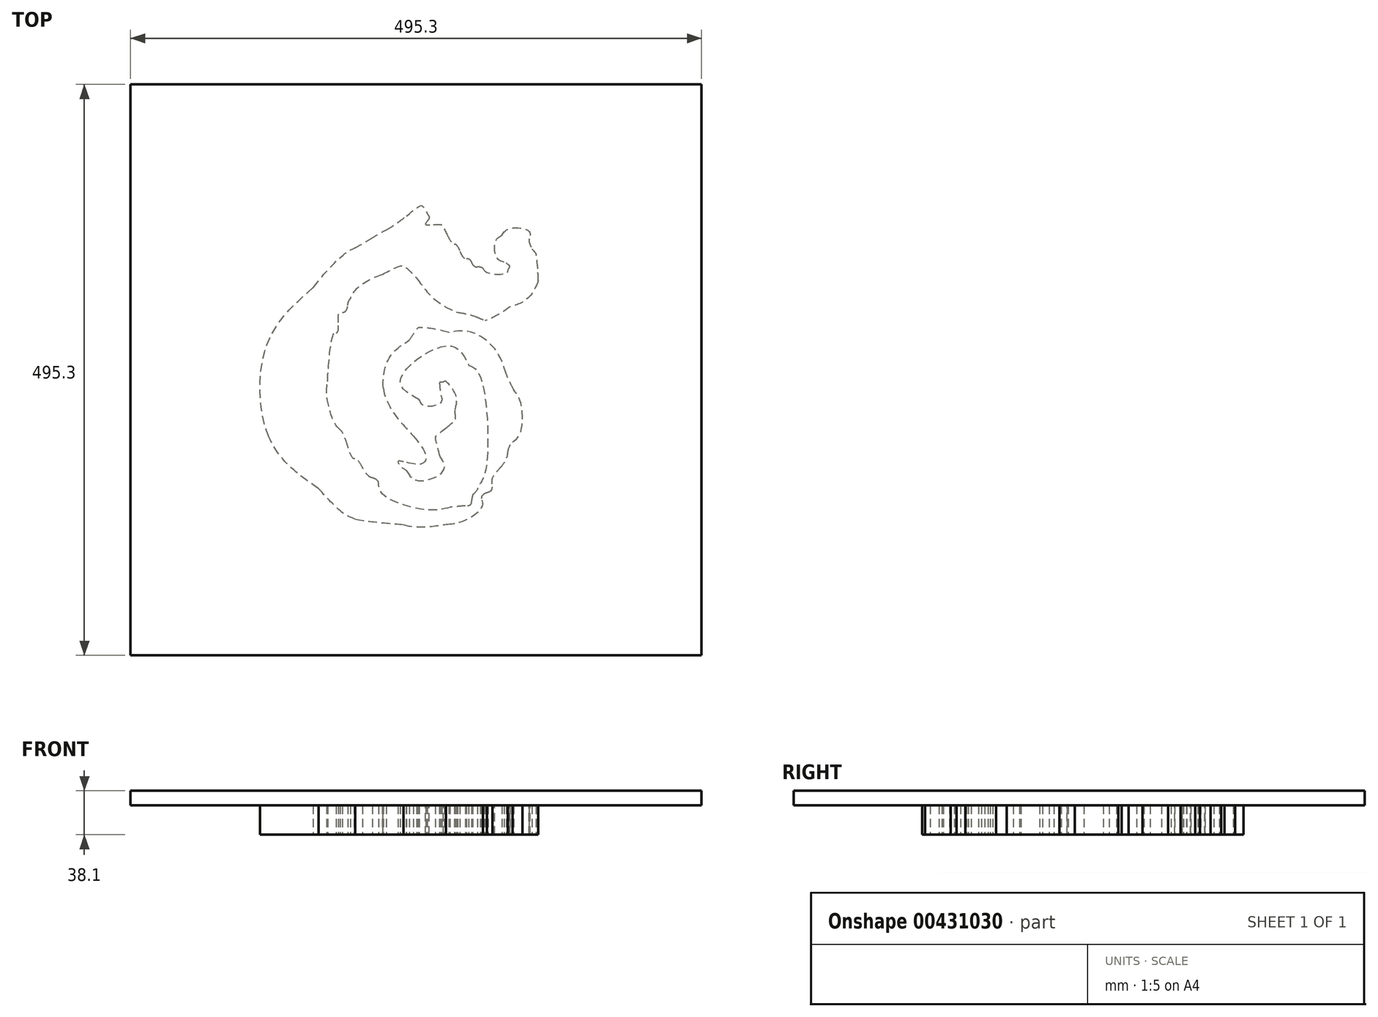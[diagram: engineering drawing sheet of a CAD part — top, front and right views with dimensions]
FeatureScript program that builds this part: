
annotation { "Feature Type Name" : "Feature", "Feature Type Description" : "" }
export const myFeature = defineFeature(function(context is Context, id is Id, definition is map)
    precondition{}
    {
        {
            var Q0;
            Q0=qCreatedBy(makeId("Top.planeOp"),FACE);
            var sketch = newSketch(context, id + "F0", { "sketchPlane" : qUnion([Q0])});
            skFitSpline(sketch, "E0", {"points": [v(-1.02, -238.68) * mm, v(-2.42, -236.97) * mm, v(-7.48, -229.69) * mm, v(-12.27, -222.5) * mm]});
            skFitSpline(sketch, "E1", {"points": [v(-12.27, -222.5) * mm, v(-17.89, -214.08) * mm, v(-22.93, -208.6) * mm, v(-26.45, -207.08) * mm]});
            skFitSpline(sketch, "E2", {"points": [v(-26.45, -207.08) * mm, v(-61.54, -191.97) * mm, v(-118.33, -161.02) * mm, v(-134.9, -147.99) * mm]});
            skFitSpline(sketch, "E3", {"points": [v(-134.9, -147.99) * mm, v(-139.85, -144.1) * mm, v(-139.85, -144.1) * mm, v(-147.93, -150.27) * mm]});
            skFitSpline(sketch, "E4", {"points": [v(-147.93, -150.27) * mm, v(-160.57, -159.92) * mm, v(-160.12, -160.27) * mm, v(-185.03, -122.21) * mm]});
            skFitSpline(sketch, "E5", {"points": [v(-185.03, -122.21) * mm, v(-197.36, -103.39) * mm, v(-210.16, -83.98) * mm, v(-213.48, -79.08) * mm]});
            skFitSpline(sketch, "E6", {"points": [v(-213.48, -79.08) * mm, v(-222.32, -66.03) * mm, v(-221.7, -63.69) * mm, v(-204.8, -46.15) * mm]});
            skFitSpline(sketch, "E7", {"points": [v(-204.8, -46.15) * mm, v(-170, -10.06) * mm, v(-147.58, 37.4) * mm, v(-143.77, 83.05) * mm]});
            skFitSpline(sketch, "E8", {"points": [v(-143.77, 83.05) * mm, v(-142.13, 102.72) * mm, v(-143.15, 105) * mm, v(-150.67, 98.45) * mm]});
            skFitSpline(sketch, "E9", {"points": [v(-150.67, 98.45) * mm, v(-167.75, 83.57) * mm, v(-171.62, 84.2) * mm, v(-178.84, 103.06) * mm]});
            skFitSpline(sketch, "E10", {"points": [v(-178.84, 103.06) * mm, v(-182.64, 112.96) * mm, v(-184.22, 117) * mm, v(-194.45, 142.84) * mm]});
            skFitSpline(sketch, "E11", {"points": [v(-194.45, 142.84) * mm, v(-200.34, 157.71) * mm, v(-201.38, 166.13) * mm, v(-197.6, 168.42) * mm]});
            skFitSpline(sketch, "E12", {"points": [v(-197.6, 168.42) * mm, v(-196.32, 169.2) * mm, v(-185.33, 180.98) * mm, v(-173.18, 194.6) * mm]});
            skFitSpline(sketch, "E13", {"points": [v(-173.18, 194.6) * mm, v(-128.58, 244.63) * mm, v(-139.54, 241.93) * mm, v(-86.43, 215.93) * mm]});
            skFitSpline(sketch, "E14", {"points": [v(-86.43, 215.93) * mm, v(6.74, 170.32) * mm, v(-14.7, 170.95) * mm, v(56.77, 211.75) * mm]});
            skFitSpline(sketch, "E15", {"points": [v(56.77, 211.75) * mm, v(63.5, 215.6) * mm, v(70.02, 218.74) * mm, v(71.24, 218.74) * mm]});
            skFitSpline(sketch, "E16", {"points": [v(71.24, 218.74) * mm, v(72.47, 218.74) * mm, v(77.4, 221.44) * mm, v(82.2, 224.73) * mm]});
            skFitSpline(sketch, "E17", {"points": [v(82.2, 224.73) * mm, v(92.15, 231.58) * mm, v(114.61, 241.85) * mm, v(119.63, 241.85) * mm]});
            skFitSpline(sketch, "E18", {"points": [v(119.63, 241.85) * mm, v(124.69, 241.85) * mm, v(189.45, 175.42) * mm, v(189.45, 170.24) * mm]});
            skFitSpline(sketch, "E19", {"points": [v(189.45, 170.24) * mm, v(189.45, 166.94) * mm, v(172.06, 112.7) * mm, v(167.23, 100.94) * mm]});
            skFitSpline(sketch, "E20", {"points": [v(167.23, 100.94) * mm, v(165.14, 95.84) * mm, v(155.87, 97.2) * mm, v(145.89, 104.07) * mm]});
            skFitSpline(sketch, "E21", {"points": [v(145.89, 104.07) * mm, v(135, 111.55) * mm, v(134.6, 110.64) * mm, v(137.92, 86.27) * mm]});
            skFitSpline(sketch, "E22", {"points": [v(137.92, 86.27) * mm, v(143.82, 42.98) * mm, v(170.3, -5.42) * mm, v(206.18, -38.48) * mm]});
            skFitSpline(sketch, "E23", {"points": [v(206.18, -38.48) * mm, v(224.34, -55.21) * mm, v(224.74, -52.07) * mm, v(198.64, -97.03) * mm]});
            skFitSpline(sketch, "E24", {"points": [v(198.64, -97.03) * mm, v(167.26, -151.07) * mm, v(166.69, -151.64) * mm, v(153.24, -142.56) * mm]});
            skFitSpline(sketch, "E25", {"points": [v(153.24, -142.56) * mm, v(145.48, -137.32) * mm, v(145.48, -137.32) * mm, v(133.58, -146.06) * mm]});
            skFitSpline(sketch, "E26", {"points": [v(133.58, -146.06) * mm, v(114.44, -160.11) * mm, v(100.57, -169.41) * mm, v(86.32, -177.74) * mm]});
            skFitSpline(sketch, "E27", {"points": [v(86.32, -177.74) * mm, v(78.99, -182.03) * mm, v(71.79, -186.45) * mm, v(70.32, -187.57) * mm]});
            skFitSpline(sketch, "E28", {"points": [v(70.32, -187.57) * mm, v(68.85, -188.68) * mm, v(62.45, -191.77) * mm, v(56.1, -194.43) * mm]});
            skFitSpline(sketch, "E29", {"points": [v(56.1, -194.43) * mm, v(32.12, -204.47) * mm, v(30.33, -205.84) * mm, v(22.3, -220.32) * mm]});
            skFitSpline(sketch, "E30", {"points": [v(22.3, -220.32) * mm, v(10.64, -241.32) * mm, v(4.86, -245.87) * mm, v(-1.02, -238.68) * mm]});
            skFitSpline(sketch, "E31", {"points": [v(16.11, -218.08) * mm, v(25.55, -201.71) * mm, v(29.54, -198.22) * mm, v(46.09, -191.83) * mm]});
            skFitSpline(sketch, "E32", {"points": [v(46.09, -191.83) * mm, v(65.73, -184.24) * mm, v(94.05, -167) * mm, v(130.03, -140.74) * mm]});
            skFitSpline(sketch, "E33", {"points": [v(130.03, -140.74) * mm, v(141.94, -132.05) * mm, v(148.89, -129.55) * mm, v(151.11, -133.15) * mm]});
            skFitSpline(sketch, "E34", {"points": [v(151.11, -133.15) * mm, v(157.57, -143.59) * mm, v(164.23, -141.9) * mm, v(172.84, -127.68) * mm]});
            skFitSpline(sketch, "E35", {"points": [v(172.84, -127.68) * mm, v(219.5, -50.54) * mm, v(217.24, -57.45) * mm, v(200.92, -42.21) * mm]});
            skFitSpline(sketch, "E36", {"points": [v(200.92, -42.21) * mm, v(158.58, -2.67) * mm, v(130.82, 54.96) * mm, v(130.78, 103.39) * mm]});
            skFitSpline(sketch, "E37", {"points": [v(130.78, 103.39) * mm, v(130.77, 119.61) * mm, v(133.52, 120.26) * mm, v(151.38, 108.2) * mm]});
            skFitSpline(sketch, "E38", {"points": [v(151.38, 108.2) * mm, v(161.7, 101.24) * mm, v(160.8, 100.02) * mm, v(173.45, 137.82) * mm]});
            skFitSpline(sketch, "E39", {"points": [v(173.45, 137.82) * mm, v(183.66, 168.37) * mm, v(183.96, 169.75) * mm, v(180.99, 173.22) * mm]});
            skFitSpline(sketch, "E40", {"points": [v(180.99, 173.22) * mm, v(129.7, 233.24) * mm, v(115.72, 240.02) * mm, v(85.72, 219.38) * mm]});
            skFitSpline(sketch, "E41", {"points": [v(85.72, 219.38) * mm, v(80.94, 216.1) * mm, v(76.03, 213.4) * mm, v(74.8, 213.4) * mm]});
            skFitSpline(sketch, "E42", {"points": [v(74.8, 213.4) * mm, v(73.57, 213.4) * mm, v(67.06, 210.26) * mm, v(60.33, 206.42) * mm]});
            skFitSpline(sketch, "E43", {"points": [v(60.33, 206.42) * mm, v(-14.7, 163.58) * mm, v(7.1, 163.08) * mm, v(-88.38, 209.84) * mm]});
            skFitSpline(sketch, "E44", {"points": [v(-88.38, 209.84) * mm, v(-136.47, 233.4) * mm, v(-128.89, 234.55) * mm, v(-160.83, 198.8) * mm]});
            skFitSpline(sketch, "E45", {"points": [v(-160.83, 198.8) * mm, v(-175.01, 182.94) * mm, v(-188.49, 168.03) * mm, v(-190.77, 165.67) * mm]});
            skFitSpline(sketch, "E46", {"points": [v(-190.77, 165.67) * mm, v(-195.4, 160.9) * mm, v(-195.25, 160.17) * mm, v(-184.76, 135.17) * mm]});
            skFitSpline(sketch, "E47", {"points": [v(-184.76, 135.17) * mm, v(-182.5, 129.79) * mm, v(-178.5, 119.79) * mm, v(-175.87, 112.94) * mm]});
            skFitSpline(sketch, "E48", {"points": [v(-175.87, 112.94) * mm, v(-167.74, 91.77) * mm, v(-167.77, 91.78) * mm, v(-153.72, 104.18) * mm]});
            skFitSpline(sketch, "E49", {"points": [v(-153.72, 104.18) * mm, v(-114.83, 138.48) * mm, v(-147.39, 4.78) * mm, v(-188.44, -38.43) * mm]});
            skFitSpline(sketch, "E50", {"points": [v(-188.44, -38.43) * mm, v(-190.37, -40.46) * mm, v(-197.05, -47.43) * mm, v(-203.28, -53.92) * mm]});
            skFitSpline(sketch, "E51", {"points": [v(-203.28, -53.92) * mm, v(-214.62, -65.72) * mm, v(-214.62, -65.72) * mm, v(-201.42, -85.74) * mm]});
            skFitSpline(sketch, "E52", {"points": [v(-201.42, -85.74) * mm, v(-194.16, -96.76) * mm, v(-181.85, -115.55) * mm, v(-174.08, -127.5) * mm]});
            skFitSpline(sketch, "E53", {"points": [v(-174.08, -127.5) * mm, v(-158.02, -152.2) * mm, v(-159.3, -151.4) * mm, v(-149.06, -143.02) * mm]});
            skFitSpline(sketch, "E54", {"points": [v(-149.06, -143.02) * mm, v(-140.94, -136.37) * mm, v(-138.43, -136.42) * mm, v(-130.44, -143.36) * mm]});
            skFitSpline(sketch, "E55", {"points": [v(-130.44, -143.36) * mm, v(-118.67, -153.6) * mm, v(-55.96, -187.61) * mm, v(-23.03, -201.64) * mm]});
            skFitSpline(sketch, "E56", {"points": [v(-23.03, -201.64) * mm, v(-17.35, -204.06) * mm, v(-13.96, -207.69) * mm, v(-6.2, -219.7) * mm]});
            skFitSpline(sketch, "E57", {"points": [v(-6.2, -219.7) * mm, v(5.38, -237.57) * mm, v(4.85, -237.6) * mm, v(16.11, -218.08) * mm]});
            skFitSpline(sketch, "E58", {"points": [v(-2.27, -208.26) * mm, v(-4.89, -205.46) * mm, v(-8.4, -201.16) * mm, v(-10.06, -198.7) * mm]});
            skFitSpline(sketch, "E59", {"points": [v(-10.06, -198.7) * mm, v(-12.06, -195.74) * mm, v(-18.68, -192) * mm, v(-29.62, -187.64) * mm]});
            skFitSpline(sketch, "E60", {"points": [v(-29.62, -187.64) * mm, v(-47.62, -180.47) * mm, v(-72.48, -167.6) * mm, v(-98.72, -151.88) * mm]});
            skFitSpline(sketch, "E61", {"points": [v(-98.72, -151.88) * mm, v(-107.95, -146.35) * mm, v(-117.78, -140.51) * mm, v(-120.57, -138.9) * mm]});
            skFitSpline(sketch, "E62", {"points": [v(-120.57, -138.9) * mm, v(-123.36, -137.3) * mm, v(-129.28, -133.14) * mm, v(-133.7, -129.65) * mm]});
            skFitSpline(sketch, "E63", {"points": [v(-133.7, -129.65) * mm, v(-141.77, -123.31) * mm, v(-141.77, -123.31) * mm, v(-145.89, -127.43) * mm]});
            skFitSpline(sketch, "E64", {"points": [v(-145.89, -127.43) * mm, v(-156.33, -137.87) * mm, v(-158.64, -136.05) * mm, v(-184.1, -97.24) * mm]});
            skFitSpline(sketch, "E65", {"points": [v(-184.1, -97.24) * mm, v(-206.54, -63.04) * mm, v(-206.22, -66.2) * mm, v(-189.14, -48.06) * mm]});
            skFitSpline(sketch, "E66", {"points": [v(-189.14, -48.06) * mm, v(-146.86, -3.14) * mm, v(-127.7, 46.35) * mm, v(-124.6, 118.61) * mm]});
            skFitSpline(sketch, "E67", {"points": [v(-124.6, 118.61) * mm, v(-123.74, 138.51) * mm, v(-123.74, 138.51) * mm, v(-134.73, 129.64) * mm]});
            skFitSpline(sketch, "E68", {"points": [v(-134.73, 129.64) * mm, v(-158.27, 110.65) * mm, v(-164.96, 109.06) * mm, v(-169.73, 121.32) * mm]});
            skFitSpline(sketch, "E69", {"points": [v(-169.73, 121.32) * mm, v(-174.94, 134.7) * mm, v(-180.9, 148.8) * mm, v(-183.24, 153.22) * mm]});
            skFitSpline(sketch, "E70", {"points": [v(-183.24, 153.22) * mm, v(-186.64, 159.67) * mm, v(-187.04, 158.78) * mm, v(-174.61, 172.25) * mm]});
            skFitSpline(sketch, "E71", {"points": [v(-174.61, 172.25) * mm, v(-168.5, 178.88) * mm, v(-157.1, 191.64) * mm, v(-149.28, 200.6) * mm]});
            skFitSpline(sketch, "E72", {"points": [v(-149.28, 200.6) * mm, v(-130.93, 221.64) * mm, v(-132.65, 221.42) * mm, v(-102.93, 206.6) * mm]});
            skFitSpline(sketch, "E73", {"points": [v(-102.93, 206.6) * mm, v(-81.26, 195.8) * mm, v(-61.19, 186.07) * mm, v(-17.08, 165) * mm]});
            skFitSpline(sketch, "E74", {"points": [v(-17.08, 165) * mm, v(-5.8, 159.6) * mm, v(-5.8, 159.6) * mm, v(0.7, 163.17) * mm]});
            skFitSpline(sketch, "E75", {"points": [v(0.7, 163.17) * mm, v(4.27, 165.13) * mm, v(16.8, 172.1) * mm, v(28.53, 178.64) * mm]});
            skFitSpline(sketch, "E76", {"points": [v(28.53, 178.64) * mm, v(53.38, 192.5) * mm, v(50.71, 191.03) * mm, v(86.78, 210.72) * mm]});
            skFitSpline(sketch, "E77", {"points": [v(86.78, 210.72) * mm, v(117.75, 227.62) * mm, v(115.7, 227.44) * mm, v(127.63, 214.3) * mm]});
            skFitSpline(sketch, "E78", {"points": [v(127.63, 214.3) * mm, v(132.07, 209.4) * mm, v(143.8, 197.17) * mm, v(153.7, 187.1) * mm]});
            skFitSpline(sketch, "E79", {"points": [v(153.7, 187.1) * mm, v(174.1, 166.36) * mm, v(173.23, 169.82) * mm, v(164.38, 144.27) * mm]});
            skFitSpline(sketch, "E80", {"points": [v(164.38, 144.27) * mm, v(161.55, 136.07) * mm, v(159.23, 127.85) * mm, v(159.23, 125.99) * mm]});
            skFitSpline(sketch, "E81", {"points": [v(159.23, 125.99) * mm, v(159.23, 117.56) * mm, v(144.8, 122.17) * mm, v(125.44, 136.77) * mm]});
            skFitSpline(sketch, "E82", {"points": [v(125.44, 136.77) * mm, v(114.03, 145.38) * mm, v(111.4, 139.7) * mm, v(114.82, 113.83) * mm]});
            skFitSpline(sketch, "E83", {"points": [v(114.82, 113.83) * mm, v(115.8, 106.5) * mm, v(116.93, 97.3) * mm, v(117.34, 93.38) * mm]});
            skFitSpline(sketch, "E84", {"points": [v(117.34, 93.38) * mm, v(122.24, 46.48) * mm, v(149.84, -4.91) * mm, v(191.48, -44.68) * mm]});
            skFitSpline(sketch, "E85", {"points": [v(191.48, -44.68) * mm, v(203.95, -56.6) * mm, v(204.2, -55.58) * mm, v(178.93, -97.73) * mm]});
            skFitSpline(sketch, "E86", {"points": [v(178.93, -97.73) * mm, v(171.02, -110.9) * mm, v(164.56, -122.3) * mm, v(164.56, -123.06) * mm]});
            skFitSpline(sketch, "E87", {"points": [v(164.56, -123.06) * mm, v(164.56, -126) * mm, v(156.61, -124.22) * mm, v(151.16, -120.06) * mm]});
            skFitSpline(sketch, "E88", {"points": [v(151.16, -120.06) * mm, v(145.42, -115.69) * mm, v(145.42, -115.69) * mm, v(142.16, -119.29) * mm]});
            skFitSpline(sketch, "E89", {"points": [v(142.16, -119.29) * mm, v(140.37, -121.27) * mm, v(133.67, -126.48) * mm, v(127.28, -130.86) * mm]});
            skFitSpline(sketch, "E90", {"points": [v(127.28, -130.86) * mm, v(120.9, -135.24) * mm, v(108.06, -144.04) * mm, v(98.77, -150.43) * mm]});
            skFitSpline(sketch, "E91", {"points": [v(98.77, -150.43) * mm, v(89.48, -156.81) * mm, v(77.48, -164.4) * mm, v(72.1, -167.3) * mm]});
            skFitSpline(sketch, "E92", {"points": [v(72.1, -167.3) * mm, v(66.72, -170.18) * mm, v(58.51, -174.9) * mm, v(53.86, -177.78) * mm]});
            skFitSpline(sketch, "E93", {"points": [v(53.86, -177.78) * mm, v(49.21, -180.66) * mm, v(40.05, -185.25) * mm, v(33.5, -187.98) * mm]});
            skFitSpline(sketch, "E94", {"points": [v(33.5, -187.98) * mm, v(24.18, -191.85) * mm, v(20.29, -194.68) * mm, v(15.7, -200.91) * mm]});
            skFitSpline(sketch, "E95", {"points": [v(15.7, -200.91) * mm, v(4.7, -215.86) * mm, v(4.8, -215.82) * mm, v(-2.27, -208.26) * mm]});
            skFitSpline(sketch, "E96", {"points": [v(13.9, -192.67) * mm, v(16.73, -189.4) * mm, v(23.55, -185.13) * mm, v(30.02, -182.54) * mm]});
            skFitSpline(sketch, "E97", {"points": [v(30.02, -182.54) * mm, v(36.19, -180.07) * mm, v(45.18, -175.61) * mm, v(50, -172.63) * mm]});
            skFitSpline(sketch, "E98", {"points": [v(50, -172.63) * mm, v(54.82, -169.65) * mm, v(63.16, -164.85) * mm, v(68.54, -161.96) * mm]});
            skFitSpline(sketch, "E99", {"points": [v(68.54, -161.96) * mm, v(73.92, -159.07) * mm, v(85.92, -151.48) * mm, v(95.21, -145.1) * mm]});
            skFitSpline(sketch, "E100", {"points": [v(95.21, -145.1) * mm, v(104.5, -138.7) * mm, v(117.33, -129.9) * mm, v(123.73, -125.52) * mm]});
            skFitSpline(sketch, "E101", {"points": [v(123.73, -125.52) * mm, v(130.12, -121.14) * mm, v(136.84, -115.9) * mm, v(138.67, -113.88) * mm]});
            skFitSpline(sketch, "E102", {"points": [v(138.67, -113.88) * mm, v(142.93, -109.18) * mm, v(147.38, -109.23) * mm, v(153.94, -114.09) * mm]});
            skFitSpline(sketch, "E103", {"points": [v(153.94, -114.09) * mm, v(156.82, -116.22) * mm, v(159.45, -117.62) * mm, v(159.78, -117.2) * mm]});
            skFitSpline(sketch, "E104", {"points": [v(159.78, -117.2) * mm, v(161.33, -115.22) * mm, v(189.3, -67.73) * mm, v(191.9, -62.66) * mm]});
            skFitSpline(sketch, "E105", {"points": [v(191.9, -62.66) * mm, v(194.87, -56.9) * mm, v(194.87, -56.9) * mm, v(186.1, -48.43) * mm]});
            skFitSpline(sketch, "E106", {"points": [v(186.1, -48.43) * mm, v(144.87, -8.65) * mm, v(117.04, 42.8) * mm, v(111.79, 88.94) * mm]});
            skFitSpline(sketch, "E107", {"points": [v(111.79, 88.94) * mm, v(111.4, 92.36) * mm, v(110.27, 101.84) * mm, v(109.28, 110) * mm]});
            skFitSpline(sketch, "E108", {"points": [v(109.28, 110) * mm, v(104.9, 146.17) * mm, v(110.45, 156.4) * mm, v(127.37, 143.34) * mm]});
            skFitSpline(sketch, "E109", {"points": [v(127.37, 143.34) * mm, v(141.62, 132.34) * mm, v(153.9, 125.9) * mm, v(153.88, 129.44) * mm]});
            skFitSpline(sketch, "E110", {"points": [v(153.88, 129.44) * mm, v(153.88, 131.12) * mm, v(156.41, 139.82) * mm, v(159.5, 148.77) * mm]});
            skFitSpline(sketch, "E111", {"points": [v(159.5, 148.77) * mm, v(166.02, 167.59) * mm, v(166.03, 167.57) * mm, v(141.17, 191.26) * mm]});
            skFitSpline(sketch, "E112", {"points": [v(141.17, 191.26) * mm, v(133.99, 198.1) * mm, v(125.1, 207.1) * mm, v(121.44, 211.23) * mm]});
            skFitSpline(sketch, "E113", {"points": [v(121.44, 211.23) * mm, v(114.77, 218.75) * mm, v(114.77, 218.75) * mm, v(92.1, 206.03) * mm]});
            skFitSpline(sketch, "E114", {"points": [v(92.1, 206.03) * mm, v(79.63, 199.04) * mm, v(66.63, 192.15) * mm, v(63.2, 190.74) * mm]});
            skFitSpline(sketch, "E115", {"points": [v(63.2, 190.74) * mm, v(59.78, 189.32) * mm, v(55.78, 187.13) * mm, v(54.32, 185.88) * mm]});
            skFitSpline(sketch, "E116", {"points": [v(54.32, 185.88) * mm, v(47.98, 180.48) * mm, v(-1.73, 154.73) * mm, v(-5.8, 154.73) * mm]});
            skFitSpline(sketch, "E117", {"points": [v(-5.8, 154.73) * mm, v(-8.28, 154.73) * mm, v(-15.17, 157.05) * mm, v(-21.11, 159.89) * mm]});
            skFitSpline(sketch, "E118", {"points": [v(-21.11, 159.89) * mm, v(-54.88, 176) * mm, v(-84.4, 190.27) * mm, v(-104.72, 200.29) * mm]});
            skFitSpline(sketch, "E119", {"points": [v(-104.72, 200.29) * mm, v(-132.68, 214.06) * mm, v(-128.8, 214.48) * mm, v(-144.83, 196.04) * mm]});
            skFitSpline(sketch, "E120", {"points": [v(-144.83, 196.04) * mm, v(-152.17, 187.6) * mm, v(-162.82, 175.74) * mm, v(-168.51, 169.66) * mm]});
            skFitSpline(sketch, "E121", {"points": [v(-168.51, 169.66) * mm, v(-177, 160.6) * mm, v(-178.55, 158.03) * mm, v(-177.13, 155.34) * mm]});
            skFitSpline(sketch, "E122", {"points": [v(-177.13, 155.34) * mm, v(-175.45, 152.17) * mm, v(-169.06, 136.86) * mm, v(-164.43, 124.94) * mm]});
            skFitSpline(sketch, "E123", {"points": [v(-164.43, 124.94) * mm, v(-163.2, 121.77) * mm, v(-161.81, 119.17) * mm, v(-161.36, 119.17) * mm]});
            skFitSpline(sketch, "E124", {"points": [v(-161.36, 119.17) * mm, v(-159.53, 119.17) * mm, v(-141.17, 132.15) * mm, v(-133.66, 138.75) * mm]});
            skFitSpline(sketch, "E125", {"points": [v(-133.66, 138.75) * mm, v(-118.96, 151.7) * mm, v(-117.72, 150.17) * mm, v(-118.9, 120.5) * mm]});
            skFitSpline(sketch, "E126", {"points": [v(-118.9, 120.5) * mm, v(-121.94, 43.56) * mm, v(-140.5, -5.52) * mm, v(-184.24, -52.37) * mm]});
            skFitSpline(sketch, "E127", {"points": [v(-184.24, -52.37) * mm, v(-191.1, -59.7) * mm, v(-196.44, -66.32) * mm, v(-196.1, -67.07) * mm]});
            skFitSpline(sketch, "E128", {"points": [v(-196.1, -67.07) * mm, v(-193.52, -72.92) * mm, v(-156.83, -126.21) * mm, v(-155.4, -126.21) * mm]});
            skFitSpline(sketch, "E129", {"points": [v(-155.4, -126.21) * mm, v(-154.38, -126.21) * mm, v(-151.7, -124.21) * mm, v(-149.43, -121.77) * mm]});
            skFitSpline(sketch, "E130", {"points": [v(-149.43, -121.77) * mm, v(-143.87, -115.77) * mm, v(-140.62, -116.15) * mm, v(-130.6, -124) * mm]});
            skFitSpline(sketch, "E131", {"points": [v(-130.6, -124) * mm, v(-125.9, -127.66) * mm, v(-119.79, -131.97) * mm, v(-117, -133.57) * mm]});
            skFitSpline(sketch, "E132", {"points": [v(-117, -133.57) * mm, v(-114.22, -135.18) * mm, v(-104.39, -141.01) * mm, v(-95.17, -146.54) * mm]});
            skFitSpline(sketch, "E133", {"points": [v(-95.17, -146.54) * mm, v(-69.58, -161.88) * mm, v(-44.12, -175.14) * mm, v(-28.37, -181.33) * mm]});
            skFitSpline(sketch, "E134", {"points": [v(-28.37, -181.33) * mm, v(-10.09, -188.52) * mm, v(-7.12, -190.52) * mm, v(-1.42, -199.55) * mm]});
            skFitSpline(sketch, "E135", {"points": [v(-1.42, -199.55) * mm, v(3.28, -207) * mm, v(3.28, -207) * mm, v(6.13, -202.66) * mm]});
            skFitSpline(sketch, "E136", {"points": [v(6.13, -202.66) * mm, v(7.7, -200.27) * mm, v(11.19, -195.77) * mm, v(13.9, -192.67) * mm]});
            skFitSpline(sketch, "E137", {"points": [v(-7.92, -138.48) * mm, v(-45.8, -128.5) * mm, v(-58.82, -121.74) * mm, v(-78.5, -101.8) * mm]});
            skFitSpline(sketch, "E138", {"points": [v(-78.5, -101.8) * mm, v(-120.65, -59.1) * mm, v(-122.87, 23.79) * mm, v(-83.18, 72.5) * mm]});
            skFitSpline(sketch, "E139", {"points": [v(-83.18, 72.5) * mm, v(-72.22, 85.94) * mm, v(-54.68, 102.81) * mm, v(-47.66, 106.66) * mm]});
            skFitSpline(sketch, "E140", {"points": [v(-47.66, 106.66) * mm, v(-43.9, 108.72) * mm, v(-37.61, 112.32) * mm, v(-33.7, 114.67) * mm]});
            skFitSpline(sketch, "E141", {"points": [v(-33.7, 114.67) * mm, v(-29.79, 117.01) * mm, v(-23.55, 120.62) * mm, v(-19.84, 122.68) * mm]});
            skFitSpline(sketch, "E142", {"points": [v(-19.84, 122.68) * mm, v(-16.12, 124.75) * mm, v(-8.22, 130.13) * mm, v(-2.28, 134.65) * mm]});
            skFitSpline(sketch, "E143", {"points": [v(-2.28, 134.65) * mm, v(8.93, 143.17) * mm, v(11.52, 143.42) * mm, v(15.96, 136.39) * mm]});
            skFitSpline(sketch, "E144", {"points": [v(15.96, 136.39) * mm, v(17.29, 134.27) * mm, v(17.27, 132.5) * mm, v(15.89, 130.28) * mm]});
            skFitSpline(sketch, "E145", {"points": [v(15.89, 130.28) * mm, v(14.15, 127.5) * mm, v(14.72, 127.17) * mm, v(21.24, 127.17) * mm]});
            skFitSpline(sketch, "E146", {"points": [v(21.24, 127.17) * mm, v(28.13, 127.17) * mm, v(28.78, 126.7) * mm, v(32.98, 118.73) * mm]});
            skFitSpline(sketch, "E147", {"points": [v(32.98, 118.73) * mm, v(35.42, 114.08) * mm, v(38.28, 110.28) * mm, v(39.32, 110.28) * mm]});
            skFitSpline(sketch, "E148", {"points": [v(39.32, 110.28) * mm, v(40.36, 110.28) * mm, v(42.55, 107.47) * mm, v(44.18, 104.05) * mm]});
            skFitSpline(sketch, "E149", {"points": [v(44.18, 104.05) * mm, v(45.81, 100.63) * mm, v(48.33, 97.83) * mm, v(49.78, 97.83) * mm]});
            skFitSpline(sketch, "E150", {"points": [v(49.78, 97.83) * mm, v(51.23, 97.83) * mm, v(53.27, 96.23) * mm, v(54.32, 94.27) * mm]});
            skFitSpline(sketch, "E151", {"points": [v(54.32, 94.27) * mm, v(55.36, 92.32) * mm, v(57.63, 90.72) * mm, v(59.36, 90.72) * mm]});
            skFitSpline(sketch, "E152", {"points": [v(59.36, 90.72) * mm, v(61.08, 90.72) * mm, v(63.26, 90.01) * mm, v(64.19, 89.16) * mm]});
            skFitSpline(sketch, "E153", {"points": [v(64.19, 89.16) * mm, v(67.96, 85.68) * mm, v(84.21, 85.1) * mm, v(86.05, 88.39) * mm]});
            skFitSpline(sketch, "E154", {"points": [v(86.05, 88.39) * mm, v(87.43, 90.86) * mm, v(86.74, 92.11) * mm, v(82.6, 94.63) * mm]});
            skFitSpline(sketch, "E155", {"points": [v(82.6, 94.63) * mm, v(76.17, 98.54) * mm, v(75, 112.85) * mm, v(80.68, 118) * mm]});
            skFitSpline(sketch, "E156", {"points": [v(80.68, 118) * mm, v(86.97, 123.69) * mm, v(104.1, 121.48) * mm, v(104.12, 114.97) * mm]});
            skFitSpline(sketch, "E157", {"points": [v(104.12, 114.97) * mm, v(104.12, 112.88) * mm, v(105.32, 108.87) * mm, v(106.78, 106.07) * mm]});
            skFitSpline(sketch, "E158", {"points": [v(106.78, 106.07) * mm, v(114.35, 91.56) * mm, v(103.88, 64.25) * mm, v(87.6, 56.03) * mm]});
            skFitSpline(sketch, "E159", {"points": [v(87.6, 56.03) * mm, v(62.2, 43.2) * mm, v(29.2, 50.39) * mm, v(4.48, 74.15) * mm]});
            skFitSpline(sketch, "E160", {"points": [v(4.48, 74.15) * mm, v(-8.04, 86.18) * mm, v(-48.81, 67.83) * mm, v(-48.81, 50.16) * mm]});
            skFitSpline(sketch, "E161", {"points": [v(-48.81, 50.16) * mm, v(-48.81, 48.32) * mm, v(-50.41, 45.37) * mm, v(-52.37, 43.6) * mm]});
            skFitSpline(sketch, "E162", {"points": [v(-52.37, 43.6) * mm, v(-54.33, 41.83) * mm, v(-55.93, 38.36) * mm, v(-55.93, 35.9) * mm]});
            skFitSpline(sketch, "E163", {"points": [v(-55.93, 35.9) * mm, v(-55.93, 33.44) * mm, v(-57.23, 29.98) * mm, v(-58.83, 28.22) * mm]});
            skFitSpline(sketch, "E164", {"points": [v(-58.83, 28.22) * mm, v(-62.06, 24.65) * mm, v(-64, -15.17) * mm, v(-61.04, -17) * mm]});
            skFitSpline(sketch, "E165", {"points": [v(-61.04, -17) * mm, v(-58.7, -18.44) * mm, v(-59.17, -24.86) * mm, v(-61.62, -24.86) * mm]});
            skFitSpline(sketch, "E166", {"points": [v(-61.62, -24.86) * mm, v(-63.28, -24.86) * mm, v(-63.28, -25.34) * mm, v(-61.62, -27) * mm]});
            skFitSpline(sketch, "E167", {"points": [v(-61.62, -27) * mm, v(-60.44, -28.17) * mm, v(-59.48, -30.87) * mm, v(-59.48, -33) * mm]});
            skFitSpline(sketch, "E168", {"points": [v(-59.48, -33) * mm, v(-59.48, -35.13) * mm, v(-58.28, -37.87) * mm, v(-56.81, -39.09) * mm]});
            skFitSpline(sketch, "E169", {"points": [v(-56.81, -39.09) * mm, v(-55.35, -40.3) * mm, v(-54.15, -42.18) * mm, v(-54.15, -43.26) * mm]});
            skFitSpline(sketch, "E170", {"points": [v(-54.15, -43.26) * mm, v(-54.15, -47.41) * mm, v(-44.6, -69.32) * mm, v(-42.75, -69.39) * mm]});
            skFitSpline(sketch, "E171", {"points": [v(-42.75, -69.39) * mm, v(-40.71, -69.47) * mm, v(-32.81, -80.81) * mm, v(-32.81, -83.66) * mm]});
            skFitSpline(sketch, "E172", {"points": [v(-32.81, -83.66) * mm, v(-32.81, -84.57) * mm, v(-31.74, -85.32) * mm, v(-30.43, -85.32) * mm]});
            skFitSpline(sketch, "E173", {"points": [v(-30.43, -85.32) * mm, v(-29.12, -85.32) * mm, v(-25.67, -87.92) * mm, v(-22.77, -91.1) * mm]});
            skFitSpline(sketch, "E174", {"points": [v(-22.77, -91.1) * mm, v(-19.86, -94.27) * mm, v(-12.73, -99.19) * mm, v(-6.92, -102.01) * mm]});
            skFitSpline(sketch, "E175", {"points": [v(-6.92, -102.01) * mm, v(-1.11, -104.84) * mm, v(5.19, -107.93) * mm, v(7.08, -108.9) * mm]});
            skFitSpline(sketch, "E176", {"points": [v(7.08, -108.9) * mm, v(12.54, -111.68) * mm, v(38.88, -112.76) * mm, v(43.33, -110.38) * mm]});
            skFitSpline(sketch, "E177", {"points": [v(43.33, -110.38) * mm, v(59.92, -101.5) * mm, v(62.04, -10.88) * mm, v(45.96, 1.77) * mm]});
            skFitSpline(sketch, "E178", {"points": [v(45.96, 1.77) * mm, v(34.77, 10.57) * mm, v(7.48, -6.12) * mm, v(12.34, -18.79) * mm]});
            skFitSpline(sketch, "E179", {"points": [v(12.34, -18.79) * mm, v(14.24, -23.72) * mm, v(21.28, -21.1) * mm, v(22.3, -15.08) * mm]});
            skFitSpline(sketch, "E180", {"points": [v(22.3, -15.08) * mm, v(23.1, -10.43) * mm, v(24.04, -9.68) * mm, v(29.71, -9.2) * mm]});
            skFitSpline(sketch, "E181", {"points": [v(29.71, -9.2) * mm, v(46.62, -7.8) * mm, v(52.59, -39.72) * mm, v(37.82, -52.57) * mm]});
            skFitSpline(sketch, "E182", {"points": [v(37.82, -52.57) * mm, v(30.22, -59.18) * mm, v(30.22, -59.18) * mm, v(31.8, -69.14) * mm]});
            skFitSpline(sketch, "E183", {"points": [v(31.8, -69.14) * mm, v(35.67, -93.53) * mm, v(9.43, -106.64) * mm, v(-8.13, -89.08) * mm]});
            skFitSpline(sketch, "E184", {"points": [v(-8.13, -89.08) * mm, v(-19, -78.21) * mm, v(-18.2, -70.55) * mm, v(-6.37, -72.12) * mm]});
            skFitSpline(sketch, "E185", {"points": [v(-6.37, -72.12) * mm, v(5.45, -73.69) * mm, v(6.01, -71.57) * mm, v(-2.58, -57.97) * mm]});
            skFitSpline(sketch, "E186", {"points": [v(-2.58, -57.97) * mm, v(-19.72, -30.83) * mm, v(-18.33, 9.35) * mm, v(0.36, 27.04) * mm]});
            skFitSpline(sketch, "E187", {"points": [v(0.36, 27.04) * mm, v(24.76, 50.13) * mm, v(73.94, 38.28) * mm, v(87.4, 6.08) * mm]});
            skFitSpline(sketch, "E188", {"points": [v(87.4, 6.08) * mm, v(88.9, 2.49) * mm, v(91.63, -2.54) * mm, v(93.46, -5.1) * mm]});
            skFitSpline(sketch, "E189", {"points": [v(93.46, -5.1) * mm, v(102.44, -17.61) * mm, v(103.32, -62.96) * mm, v(94.68, -67.8) * mm]});
            skFitSpline(sketch, "E190", {"points": [v(94.68, -67.8) * mm, v(93.24, -68.6) * mm, v(91.55, -72) * mm, v(90.92, -75.33) * mm]});
            skFitSpline(sketch, "E191", {"points": [v(90.92, -75.33) * mm, v(90.3, -78.67) * mm, v(88.6, -82.38) * mm, v(87.17, -83.58) * mm]});
            skFitSpline(sketch, "E192", {"points": [v(87.17, -83.58) * mm, v(85.72, -84.77) * mm, v(84.54, -86.73) * mm, v(84.54, -87.93) * mm]});
            skFitSpline(sketch, "E193", {"points": [v(84.54, -87.93) * mm, v(84.54, -89.12) * mm, v(82.94, -91.55) * mm, v(80.99, -93.32) * mm]});
            skFitSpline(sketch, "E194", {"points": [v(80.99, -93.32) * mm, v(79.03, -95.09) * mm, v(77.43, -98.66) * mm, v(77.43, -101.26) * mm]});
            skFitSpline(sketch, "E195", {"points": [v(77.43, -101.26) * mm, v(77.43, -103.86) * mm, v(75.83, -107.7) * mm, v(73.88, -109.8) * mm]});
            skFitSpline(sketch, "E196", {"points": [v(73.88, -109.8) * mm, v(71.92, -111.9) * mm, v(70.31, -114.25) * mm, v(70.3, -115.03) * mm]});
            skFitSpline(sketch, "E197", {"points": [v(70.3, -115.03) * mm, v(70.28, -116.89) * mm, v(60.28, -126.28) * mm, v(52.82, -131.46) * mm]});
            skFitSpline(sketch, "E198", {"points": [v(52.82, -131.46) * mm, v(42.15, -138.86) * mm, v(8.36, -142.77) * mm, v(-7.92, -138.48) * mm]});
            skFitSpline(sketch, "E199", {"points": [v(32.1, -132.58) * mm, v(45.54, -130.47) * mm, v(63.2, -117.88) * mm, v(63.2, -110.4) * mm]});
            skFitSpline(sketch, "E200", {"points": [v(63.2, -110.4) * mm, v(63.2, -108.66) * mm, v(65.2, -106.31) * mm, v(67.65, -105.2) * mm]});
            skFitSpline(sketch, "E201", {"points": [v(67.65, -105.2) * mm, v(71, -103.67) * mm, v(72.1, -101.82) * mm, v(72.1, -97.66) * mm]});
            skFitSpline(sketch, "E202", {"points": [v(72.1, -97.66) * mm, v(72.1, -93.99) * mm, v(74.18, -89.6) * mm, v(78.31, -84.56) * mm]});
            skFitSpline(sketch, "E203", {"points": [v(78.31, -84.56) * mm, v(81.73, -80.39) * mm, v(85.04, -74.25) * mm, v(85.67, -70.92) * mm]});
            skFitSpline(sketch, "E204", {"points": [v(85.67, -70.92) * mm, v(86.3, -67.6) * mm, v(88.1, -63.4) * mm, v(89.68, -61.6) * mm]});
            skFitSpline(sketch, "E205", {"points": [v(89.68, -61.6) * mm, v(96.38, -53.93) * mm, v(97, -27.7) * mm, v(90.74, -15.97) * mm]});
            skFitSpline(sketch, "E206", {"points": [v(90.74, -15.97) * mm, v(89.44, -13.53) * mm, v(86.6, -7.53) * mm, v(84.42, -2.64) * mm]});
            skFitSpline(sketch, "E207", {"points": [v(84.42, -2.64) * mm, v(74.98, 18.6) * mm, v(54.02, 33.86) * mm, v(34.43, 33.78) * mm]});
            skFitSpline(sketch, "E208", {"points": [v(34.43, 33.78) * mm, v(-6.27, 33.6) * mm, v(-22.5, -13.94) * mm, v(3.75, -56.07) * mm]});
            skFitSpline(sketch, "E209", {"points": [v(3.75, -56.07) * mm, v(14.43, -73.2) * mm, v(11.87, -79.9) * mm, v(-4.8, -78.5) * mm]});
            skFitSpline(sketch, "E210", {"points": [v(-4.8, -78.5) * mm, v(-9.45, -78.12) * mm, v(-8.58, -80.89) * mm, v(-2.45, -86.05) * mm]});
            skFitSpline(sketch, "E211", {"points": [v(-2.45, -86.05) * mm, v(8.1, -94.92) * mm, v(29.95, -85.92) * mm, v(26.96, -73.93) * mm]});
            skFitSpline(sketch, "E212", {"points": [v(26.96, -73.93) * mm, v(23.01, -58.06) * mm, v(23.36, -56.36) * mm, v(31.96, -49.22) * mm]});
            skFitSpline(sketch, "E213", {"points": [v(31.96, -49.22) * mm, v(39.74, -42.76) * mm, v(40.09, -42.06) * mm, v(40.03, -33.22) * mm]});
            skFitSpline(sketch, "E214", {"points": [v(40.03, -33.22) * mm, v(39.93, -19.14) * mm, v(27.86, -6.85) * mm, v(27.67, -20.64) * mm]});
            skFitSpline(sketch, "E215", {"points": [v(27.67, -20.64) * mm, v(27.58, -27.09) * mm, v(13.79, -30.18) * mm, v(8.96, -24.84) * mm]});
            skFitSpline(sketch, "E216", {"points": [v(8.96, -24.84) * mm, v(-7.35, -6.82) * mm, v(33.82, 22.11) * mm, v(51.77, 5.25) * mm]});
            skFitSpline(sketch, "E217", {"points": [v(51.77, 5.25) * mm, v(61.44, -3.83) * mm, v(66.26, -86.6) * mm, v(57.98, -101.32) * mm]});
            skFitSpline(sketch, "E218", {"points": [v(57.98, -101.32) * mm, v(56.6, -103.77) * mm, v(54.98, -108.17) * mm, v(54.38, -111.1) * mm]});
            skFitSpline(sketch, "E219", {"points": [v(54.38, -111.1) * mm, v(53.55, -115.17) * mm, v(52.25, -116.5) * mm, v(48.91, -116.71) * mm]});
            skFitSpline(sketch, "E220", {"points": [v(48.91, -116.71) * mm, v(46.5, -116.86) * mm, v(40.54, -117.44) * mm, v(35.65, -117.99) * mm]});
            skFitSpline(sketch, "E221", {"points": [v(35.65, -117.99) * mm, v(15.56, -120.24) * mm, v(-22.35, -107.27) * mm, v(-26.38, -96.77) * mm]});
            skFitSpline(sketch, "E222", {"points": [v(-26.38, -96.77) * mm, v(-26.93, -95.33) * mm, v(-29.36, -93.4) * mm, v(-31.78, -92.49) * mm]});
            skFitSpline(sketch, "E223", {"points": [v(-31.78, -92.49) * mm, v(-34.2, -91.57) * mm, v(-38, -87.62) * mm, v(-40.25, -83.72) * mm]});
            skFitSpline(sketch, "E224", {"points": [v(-40.25, -83.72) * mm, v(-42.5, -79.81) * mm, v(-45.55, -76.3) * mm, v(-47.02, -75.91) * mm]});
            skFitSpline(sketch, "E225", {"points": [v(-47.02, -75.91) * mm, v(-48.5, -75.52) * mm, v(-51.27, -70.58) * mm, v(-53.18, -64.92) * mm]});
            skFitSpline(sketch, "E226", {"points": [v(-53.18, -64.92) * mm, v(-55.1, -59.27) * mm, v(-58.06, -52.85) * mm, v(-59.79, -50.66) * mm]});
            skFitSpline(sketch, "E227", {"points": [v(-59.79, -50.66) * mm, v(-65.22, -43.75) * mm, v(-71.33, -20.25) * mm, v(-70.65, -8.86) * mm]});
            skFitSpline(sketch, "E228", {"points": [v(-70.65, -8.86) * mm, v(-69.77, 6) * mm, v(-65.14, 32.82) * mm, v(-63.35, 33.42) * mm]});
            skFitSpline(sketch, "E229", {"points": [v(-63.35, 33.42) * mm, v(-62.16, 33.81) * mm, v(-61.26, 37.57) * mm, v(-61.26, 42.13) * mm]});
            skFitSpline(sketch, "E230", {"points": [v(-61.26, 42.13) * mm, v(-61.26, 48.58) * mm, v(-60.58, 50.33) * mm, v(-57.8, 51.06) * mm]});
            skFitSpline(sketch, "E231", {"points": [v(-57.8, 51.06) * mm, v(-55.77, 51.59) * mm, v(-53.87, 54.13) * mm, v(-53.2, 57.23) * mm]});
            skFitSpline(sketch, "E232", {"points": [v(-53.2, 57.23) * mm, v(-52.56, 60.13) * mm, v(-50.95, 62.92) * mm, v(-49.61, 63.43) * mm]});
            skFitSpline(sketch, "E233", {"points": [v(-49.61, 63.43) * mm, v(-48.28, 63.95) * mm, v(-44.16, 67.23) * mm, v(-40.45, 70.74) * mm]});
            skFitSpline(sketch, "E234", {"points": [v(-40.45, 70.74) * mm, v(-33.28, 77.51) * mm, v(-5.46, 91.6) * mm, v(-2.67, 89.88) * mm]});
            skFitSpline(sketch, "E235", {"points": [v(-2.67, 89.88) * mm, v(-1.75, 89.31) * mm, v(2.44, 85.22) * mm, v(6.65, 80.8) * mm]});
            skFitSpline(sketch, "E236", {"points": [v(6.65, 80.8) * mm, v(28.44, 57.86) * mm, v(66.23, 48.02) * mm, v(81.05, 61.43) * mm]});
            skFitSpline(sketch, "E237", {"points": [v(81.05, 61.43) * mm, v(82.85, 63.06) * mm, v(85.1, 63.9) * mm, v(86.06, 63.32) * mm]});
            skFitSpline(sketch, "E238", {"points": [v(86.06, 63.32) * mm, v(93.94, 58.45) * mm, v(106.1, 90.84) * mm, v(101.03, 103.16) * mm]});
            skFitSpline(sketch, "E239", {"points": [v(101.03, 103.16) * mm, v(100.02, 105.6) * mm, v(98.9, 109.2) * mm, v(98.52, 111.16) * mm]});
            skFitSpline(sketch, "E240", {"points": [v(98.52, 111.16) * mm, v(98.08, 113.52) * mm, v(96.18, 114.91) * mm, v(92.87, 115.3) * mm]});
            skFitSpline(sketch, "E241", {"points": [v(92.87, 115.3) * mm, v(81.37, 116.61) * mm, v(78.58, 104.2) * mm, v(88.99, 98.06) * mm]});
            skFitSpline(sketch, "E242", {"points": [v(88.99, 98.06) * mm, v(96.09, 93.88) * mm, v(96.24, 93.32) * mm, v(92.4, 85.64) * mm]});
            skFitSpline(sketch, "E243", {"points": [v(92.4, 85.64) * mm, v(86.9, 74.59) * mm, v(58.5, 79.41) * mm, v(44.07, 93.85) * mm]});
            skFitSpline(sketch, "E244", {"points": [v(44.07, 93.85) * mm, v(40.26, 97.66) * mm, v(35.81, 101.28) * mm, v(34.18, 101.9) * mm]});
            skFitSpline(sketch, "E245", {"points": [v(34.18, 101.9) * mm, v(32.54, 102.54) * mm, v(31.2, 104.3) * mm, v(31.2, 105.84) * mm]});
            skFitSpline(sketch, "E246", {"points": [v(31.2, 105.84) * mm, v(31.2, 115.98) * mm, v(20.82, 125.86) * mm, v(15.63, 120.66) * mm]});
            skFitSpline(sketch, "E247", {"points": [v(15.63, 120.66) * mm, v(12.6, 117.63) * mm, v(8.42, 121.75) * mm, v(7.74, 128.44) * mm]});
            skFitSpline(sketch, "E248", {"points": [v(7.74, 128.44) * mm, v(7.2, 133.9) * mm, v(7.2, 133.9) * mm, v(-1.15, 127.5) * mm]});
            skFitSpline(sketch, "E249", {"points": [v(-1.15, 127.5) * mm, v(-5.75, 123.99) * mm, v(-12.55, 119.44) * mm, v(-16.27, 117.39) * mm]});
            skFitSpline(sketch, "E250", {"points": [v(-16.27, 117.39) * mm, v(-29.51, 110.08) * mm, v(-33.71, 107.6) * mm, v(-34.59, 106.51) * mm]});
            skFitSpline(sketch, "E251", {"points": [v(-34.59, 106.51) * mm, v(-35.08, 105.91) * mm, v(-38.84, 103.71) * mm, v(-42.95, 101.63) * mm]});
            skFitSpline(sketch, "E252", {"points": [v(-42.95, 101.63) * mm, v(-63.92, 91) * mm, v(-92.57, 53.13) * mm, v(-100.43, 25.64) * mm]});
            skFitSpline(sketch, "E253", {"points": [v(-100.43, 25.64) * mm, v(-122.37, -51.1) * mm, v(-84.24, -114.23) * mm, v(-4.69, -132.89) * mm]});
            skFitSpline(sketch, "E254", {"points": [v(-4.69, -132.89) * mm, v(2.57, -134.6) * mm, v(20.18, -134.44) * mm, v(32.1, -132.58) * mm]});
            skLineSegment(sketch, "E255.bottom", {"start": v(-253.35, 252.16) * mm, "end": v(251.57, 252.16) * mm});
            skLineSegment(sketch, "E255.top", {"start": v(-253.35, -248.6) * mm, "end": v(251.57, -248.6) * mm});
            skLineSegment(sketch, "E255.left", {"start": v(-253.35, 252.16) * mm, "end": v(-253.35, -248.6) * mm});
            skLineSegment(sketch, "E255.right", {"start": v(251.57, 252.16) * mm, "end": v(251.57, -248.6) * mm});
            skSolve(sketch);
        }
        {
            var Q0;
            Q0=makeQuery(id+"F0.imprint","IMPRINT",FACE,{"disambiguationData":[TD([[makeQuery(id+"F0.imprint","IMPRINT",EDGE,{"derivedFrom":sQuery(id+"F0.wireOp",EDGE,"E199")}),1.0]])]});
            var Q1;
            Q1=makeQuery(id+"F0.imprint","IMPRINT",FACE,{"disambiguationData":[TD([[makeQuery(id+"F0.imprint","IMPRINT",EDGE,{"derivedFrom":sQuery(id+"F0.wireOp",EDGE,"E31")}),1.0]])]});
            var Q2;
            Q2=makeQuery(id+"F0.imprint","IMPRINT",FACE,{"disambiguationData":[TD([[makeQuery(id+"F0.imprint","IMPRINT",EDGE,{"derivedFrom":sQuery(id+"F0.wireOp",EDGE,"E58")}),-1.0]])]});
            var Q3;
            Q3=makeQuery(id+"F0.imprint","IMPRINT",FACE,{"disambiguationData":[TD([[makeQuery(id+"F0.imprint","IMPRINT",EDGE,{"derivedFrom":sQuery(id+"F0.wireOp",EDGE,"E0")}),-1.0]])]});
            extrude(context, id + "F1", {"entities" : qUnion([Q0, Q1, Q2, Q3]), "depth" : 25.4 * mm});
        }
        {
            var Q0;
            Q0=makeQuery(id+"F1.opExtrude","CAP_FACE",FACE,{"disambiguationData":[OSD([sQuery(id+"F0.wireOp",EDGE,"E0"),sQuery(id+"F0.wireOp",EDGE,"E1"),sQuery(id+"F0.wireOp",EDGE,"E2"),sQuery(id+"F0.wireOp",EDGE,"E3"),sQuery(id+"F0.wireOp",EDGE,"E4"),sQuery(id+"F0.wireOp",EDGE,"E5"),sQuery(id+"F0.wireOp",EDGE,"E6"),sQuery(id+"F0.wireOp",EDGE,"E7"),sQuery(id+"F0.wireOp",EDGE,"E8"),sQuery(id+"F0.wireOp",EDGE,"E9"),sQuery(id+"F0.wireOp",EDGE,"E10"),sQuery(id+"F0.wireOp",EDGE,"E11"),sQuery(id+"F0.wireOp",EDGE,"E12"),sQuery(id+"F0.wireOp",EDGE,"E13"),sQuery(id+"F0.wireOp",EDGE,"E14"),sQuery(id+"F0.wireOp",EDGE,"E15"),sQuery(id+"F0.wireOp",EDGE,"E16"),sQuery(id+"F0.wireOp",EDGE,"E17"),sQuery(id+"F0.wireOp",EDGE,"E18"),sQuery(id+"F0.wireOp",EDGE,"E19"),sQuery(id+"F0.wireOp",EDGE,"E20"),sQuery(id+"F0.wireOp",EDGE,"E21"),sQuery(id+"F0.wireOp",EDGE,"E22"),sQuery(id+"F0.wireOp",EDGE,"E23"),sQuery(id+"F0.wireOp",EDGE,"E24"),sQuery(id+"F0.wireOp",EDGE,"E25"),sQuery(id+"F0.wireOp",EDGE,"E26"),sQuery(id+"F0.wireOp",EDGE,"E27"),sQuery(id+"F0.wireOp",EDGE,"E28"),sQuery(id+"F0.wireOp",EDGE,"E29"),sQuery(id+"F0.wireOp",EDGE,"E30"),sQuery(id+"F0.wireOp",EDGE,"E96"),sQuery(id+"F0.wireOp",EDGE,"E97"),sQuery(id+"F0.wireOp",EDGE,"E98"),sQuery(id+"F0.wireOp",EDGE,"E99"),sQuery(id+"F0.wireOp",EDGE,"E100"),sQuery(id+"F0.wireOp",EDGE,"E101"),sQuery(id+"F0.wireOp",EDGE,"E102"),sQuery(id+"F0.wireOp",EDGE,"E103"),sQuery(id+"F0.wireOp",EDGE,"E104"),sQuery(id+"F0.wireOp",EDGE,"E105"),sQuery(id+"F0.wireOp",EDGE,"E106"),sQuery(id+"F0.wireOp",EDGE,"E107"),sQuery(id+"F0.wireOp",EDGE,"E108"),sQuery(id+"F0.wireOp",EDGE,"E109"),sQuery(id+"F0.wireOp",EDGE,"E110"),sQuery(id+"F0.wireOp",EDGE,"E111"),sQuery(id+"F0.wireOp",EDGE,"E112"),sQuery(id+"F0.wireOp",EDGE,"E113"),sQuery(id+"F0.wireOp",EDGE,"E114"),sQuery(id+"F0.wireOp",EDGE,"E115"),sQuery(id+"F0.wireOp",EDGE,"E116"),sQuery(id+"F0.wireOp",EDGE,"E117"),sQuery(id+"F0.wireOp",EDGE,"E118"),sQuery(id+"F0.wireOp",EDGE,"E119"),sQuery(id+"F0.wireOp",EDGE,"E120"),sQuery(id+"F0.wireOp",EDGE,"E121"),sQuery(id+"F0.wireOp",EDGE,"E122"),sQuery(id+"F0.wireOp",EDGE,"E123"),sQuery(id+"F0.wireOp",EDGE,"E124"),sQuery(id+"F0.wireOp",EDGE,"E125"),sQuery(id+"F0.wireOp",EDGE,"E126"),sQuery(id+"F0.wireOp",EDGE,"E127"),sQuery(id+"F0.wireOp",EDGE,"E128"),sQuery(id+"F0.wireOp",EDGE,"E129"),sQuery(id+"F0.wireOp",EDGE,"E130"),sQuery(id+"F0.wireOp",EDGE,"E131"),sQuery(id+"F0.wireOp",EDGE,"E132"),sQuery(id+"F0.wireOp",EDGE,"E133"),sQuery(id+"F0.wireOp",EDGE,"E134"),sQuery(id+"F0.wireOp",EDGE,"E135"),sQuery(id+"F0.wireOp",EDGE,"E136")])],"isStart":false});
            var sketch = newSketch(context, id + "F2", { "sketchPlane" : qUnion([Q0])});
            skLineSegment(sketch, "E256.bottom", {"start": v(-241.57, 248.85) * mm, "end": v(253.73, 248.85) * mm});
            skLineSegment(sketch, "E256.top", {"start": v(-241.57, -246.45) * mm, "end": v(253.73, -246.45) * mm});
            skLineSegment(sketch, "E256.left", {"start": v(-241.57, 248.85) * mm, "end": v(-241.57, -246.45) * mm});
            skLineSegment(sketch, "E256.right", {"start": v(253.73, 248.85) * mm, "end": v(253.73, -246.45) * mm});
            skSolve(sketch);
        }
        {
            var Q0;
            Q0 = qSketchRegion(id + "F2", true);
            extrude(context, id + "F3", {"entities" : qUnion([Q0]), "depth" : 12.7 * mm});
        }
    });
